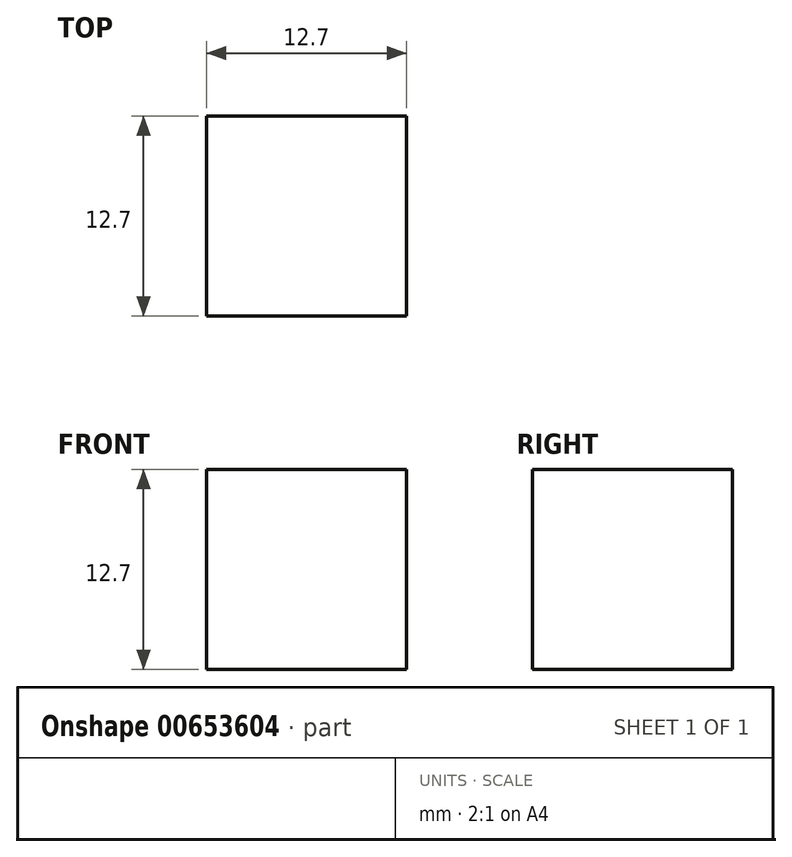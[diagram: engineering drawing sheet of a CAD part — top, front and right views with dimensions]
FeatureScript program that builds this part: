
annotation { "Feature Type Name" : "Feature", "Feature Type Description" : "" }
export const myFeature = defineFeature(function(context is Context, id is Id, definition is map)
    precondition{}
    {
        {
            var Q0;
            Q0=qCreatedBy(makeId("Front.planeOp"),FACE);
            var sketch = newSketch(context, id + "F0", { "sketchPlane" : qUnion([Q0])});
            skLineSegment(sketch, "E0", {"start": v(0, 0) * mm, "end": v(0, 12.7) * mm});
            skLineSegment(sketch, "E1", {"start": v(0, 12.7) * mm, "end": v(12.7, 12.7) * mm});
            skLineSegment(sketch, "E2", {"start": v(12.7, 12.7) * mm, "end": v(12.7, 0) * mm});
            skLineSegment(sketch, "E3", {"start": v(12.7, 0) * mm, "end": v(0, 0) * mm});
            skSolve(sketch);
        }
        {
            var Q0;
            Q0 = qSketchRegion(id + "F0", true);
            extrude(context, id + "F1", {"entities" : qUnion([Q0]), "depth" : 12.7 * mm, "offsetDistance" : 25.4 * mm});
        }
    });
